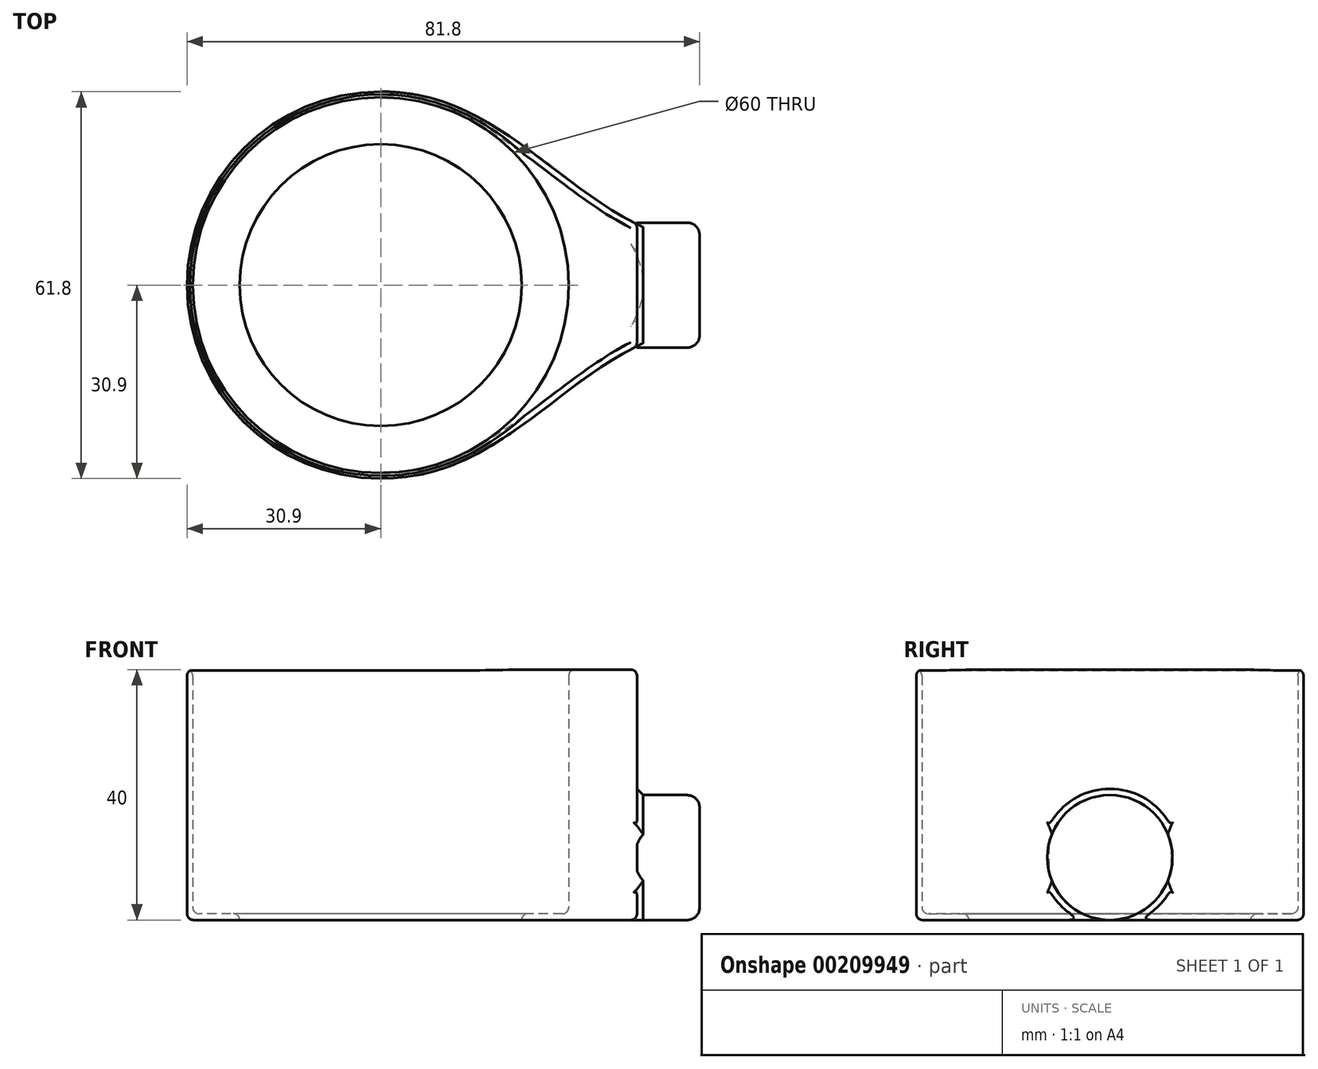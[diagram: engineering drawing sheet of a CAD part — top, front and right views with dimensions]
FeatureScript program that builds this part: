
annotation { "Feature Type Name" : "Feature", "Feature Type Description" : "" }
export const myFeature = defineFeature(function(context is Context, id is Id, definition is map)
    precondition{}
    {
        {
            var Q0;
            Q0=qCreatedBy(makeId("Right.planeOp"),FACE);
            var sketch = newSketch(context, id + "F0", { "sketchPlane" : qUnion([Q0])});
            skCircle(sketch, "E0", {"center": v(0, 0) * mm, "radius": 9.97 * mm});
            skSolve(sketch);
        }
        {
            var Q0;
            Q0=makeQuery(id+"F0.imprint","IMPRINT",FACE,{"disambiguationData":[TD([[makeQuery(id+"F0.imprint","IMPRINT",EDGE,{"derivedFrom":sQuery(id+"F0.wireOp",EDGE,"E0")}),1.0]])]});
            extrude(context, id + "F1", {"entities" : qUnion([Q0]), "depth" : 10 * mm});
        }
        {
            var Q0;
            Q0=qCreatedBy(makeId("Top.planeOp"),FACE);
            var sketch = newSketch(context, id + "F2", { "sketchPlane" : qUnion([Q0])});
            skCircle(sketch, "E1", {"center": v(-40.9, 0) * mm, "radius": 30.9 * mm});
            skLineSegment(sketch, "E2", {"start": v(-40.9, 0) * mm, "end": v(-40.9, 30.9) * mm, "construction": true});
            skLineSegment(sketch, "E3", {"start": v(-40.9, 0) * mm, "end": v(-40.9, -30.9) * mm, "construction": true});
            skCircle(sketch, "E4", {"center": v(-40.9, 0) * mm, "radius": 9.75 * mm, "construction": true});
            skPoint(sketch, "E5", {"position": v(-40.9, 9.75) * mm});
            skPoint(sketch, "E6", {"position": v(-40.9, -9.75) * mm});
            skFitSpline(sketch, "E7", {"points": [v(-40.9, 30.9) * mm, v(0, 9.75) * mm], "startDerivative": vector(52.12, 0.26) * mm, "endDerivative": vector(41.55, -20.66) * mm});
            skLineSegment(sketch, "E8", {"start": v(-40.9, 0) * mm, "end": v(-10, 0) * mm, "construction": true});
            skFitSpline(sketch, "E9.MirrorCS", {"points": [v(-40.9, -30.9) * mm, v(0, -9.75) * mm], "startDerivative": vector(52.12, -0.26) * mm, "endDerivative": vector(41.55, 20.66) * mm});
            skLineSegment(sketch, "E10", {"start": v(0, -9.75) * mm, "end": v(0, 9.75) * mm});
            skCircle(sketch, "E11", {"center": v(-40.9, 0) * mm, "radius": 30 * mm});
            skCircle(sketch, "E12", {"center": v(-40.9, 0) * mm, "radius": 22.5 * mm});
            skSolve(sketch);
        }
        {
            var Q0;
            Q0=makeQuery(id+"F1.opExtrude","SWEPT_BODY",BODY,{"disambiguationData":[OSD([sQuery(id+"F0.wireOp",EDGE,"E0")])]});
            transform(context, id + "F3", {"entities" : qUnion([Q0]), "transformType" : TransformType.TRANSLATION_3D, "dx" : 0 * mm, "dy" : 0 * mm, "dz" : (19.95 / 2) * mm, "makeCopy" : false});
        }
        {
            var Q0;
            Q0=makeQuery(id+"F2.imprint","IMPRINT",FACE,{"disambiguationData":[TD([[makeQuery(id+"F2.imprint","IMPRINT",EDGE,{"derivedFrom":sQuery(id+"F2.wireOp",EDGE,"E11")}),1.0]])]});
            extrude(context, id + "F4", {"entities" : qUnion([Q0]), "depth" : 1 * mm});
        }
        {
            var Q0;
            Q0=makeQuery(id+"F2.imprint","IMPRINT",FACE,{"disambiguationData":[TD([[makeQuery(id+"F2.imprint","IMPRINT",EDGE,{"derivedFrom":sQuery(id+"F2.wireOp",EDGE,"E11")}),-1.0]])]});
            var Q1;
            {var subQ0=sQuery(id+"F2.wireOp",EDGE,"E7");Q1=makeQuery(id+"F2.imprint","IMPRINT",FACE,{"disambiguationData":[TD([[makeQuery(id+"F2.imprint","IMPRINT",EDGE,{"derivedFrom":subQ0}),-1.0]])]});}
            extrude(context, id + "F5", {"entities" : qUnion([Q0, Q1]), "operationType" : NewBodyOperationType.ADD, "depth" : 40 * mm});
        }
        {
            var Q0;
            Q0=makeQuery(id+"F1.opExtrude","CAP_FACE",FACE,{"disambiguationData":[OSD([sQuery(id+"F0.wireOp",EDGE,"E0")])],"isStart":false});
            fillet(context, id + "F6", {"entities" : qUnion([Q0]), "radius" : 2 * mm, "tangentPropagation" : true, "allowEdgeOverflow" : false});
        }
        {
            var Q0;
            {var subQ0=sQuery(id+"F0.wireOp",EDGE,"E0");var subQ1=makeQuery(id+"F1.opExtrude","SWEPT_FACE",FACE,{"disambiguationData":[OSD([subQ0])]});var subQ2=makeQuery(id+"F5.opExtrude","SWEPT_FACE",FACE,{"disambiguationData":[OSD([sQuery(id+"F2.wireOp",EDGE,"E10")])]});Q0=makeQuery(id+"F5.boolean.opBoolean","SPLIT",EDGE,{"disambiguationData":[topologyDisambiguationEdgeConnected([subQ1,subQ2]),TD([subQ1,makeQuery(id+"F1.opExtrude","CAP_FACE",FACE,{"disambiguationData":[OSD([subQ0])],"isStart":true}),makeQuery(id+"F5.opExtrude","SWEPT_FACE",FACE,{"disambiguationData":[OSD([sQuery(id+"F2.wireOp",EDGE,"E7")])]}),makeQuery(id+"F5.opExtrude","SWEPT_FACE",FACE,{"disambiguationData":[OSD([sQuery(id+"F2.wireOp",EDGE,"E9.MirrorCS")])]}),subQ2])],"derivedFrom":makeQuery(id+"F1.opExtrude","CAP_EDGE",EDGE,{"disambiguationData":[OSD([subQ0])],"isStart":true})});}
            var Q1;
            {var subQ0=sQuery(id+"F2.wireOp",EDGE,"E11");var subQ1=sQuery(id+"F2.wireOp",EDGE,"E10");var subQ2=sQuery(id+"F2.wireOp",EDGE,"E7");var subQ3=sQuery(id+"F0.wireOp",EDGE,"E0");var subQ4=makeQuery(id+"F1.opExtrude","SWEPT_FACE",FACE,{"disambiguationData":[OSD([subQ3])]});var subQ5=makeQuery(id+"F5.opExtrude","SWEPT_FACE",FACE,{"disambiguationData":[OSD([subQ1])]});Q1=makeQuery(id+"F5.boolean.opBoolean","SPLIT",EDGE,{"disambiguationData":[topologyDisambiguationEdgeConnected([subQ4,subQ5]),TD([subQ4,makeQuery(id+"F1.opExtrude","CAP_FACE",FACE,{"disambiguationData":[OSD([subQ3])],"isStart":true}),makeQuery(id+"F4.opExtrude","CAP_FACE",FACE,{"disambiguationData":[OSD([subQ0,sQuery(id+"F2.wireOp",EDGE,"E12")])],"isStart":true}),makeQuery(id+"F5.opExtrude","CAP_FACE",FACE,{"disambiguationData":[OSD([sQuery(id+"F2.wireOp",EDGE,"E1"),subQ2,sQuery(id+"F2.wireOp",EDGE,"E9.MirrorCS"),subQ1,subQ0])],"isStart":true}),makeQuery(id+"F5.opExtrude","SWEPT_FACE",FACE,{"disambiguationData":[OSD([subQ2])]}),subQ5])],"derivedFrom":makeQuery(id+"F1.opExtrude","CAP_EDGE",EDGE,{"disambiguationData":[OSD([subQ3])],"isStart":true})});}
            var Q2;
            {var subQ0=sQuery(id+"F2.wireOp",EDGE,"E11");var subQ1=sQuery(id+"F2.wireOp",EDGE,"E10");var subQ2=sQuery(id+"F2.wireOp",EDGE,"E9.MirrorCS");var subQ3=sQuery(id+"F0.wireOp",EDGE,"E0");var subQ4=makeQuery(id+"F1.opExtrude","SWEPT_FACE",FACE,{"disambiguationData":[OSD([subQ3])]});var subQ5=makeQuery(id+"F5.opExtrude","SWEPT_FACE",FACE,{"disambiguationData":[OSD([subQ1])]});Q2=makeQuery(id+"F5.boolean.opBoolean","SPLIT",EDGE,{"disambiguationData":[topologyDisambiguationEdgeConnected([subQ4,subQ5]),TD([subQ4,makeQuery(id+"F1.opExtrude","CAP_FACE",FACE,{"disambiguationData":[OSD([subQ3])],"isStart":true}),makeQuery(id+"F4.opExtrude","CAP_FACE",FACE,{"disambiguationData":[OSD([subQ0,sQuery(id+"F2.wireOp",EDGE,"E12")])],"isStart":true}),makeQuery(id+"F5.opExtrude","CAP_FACE",FACE,{"disambiguationData":[OSD([sQuery(id+"F2.wireOp",EDGE,"E1"),sQuery(id+"F2.wireOp",EDGE,"E7"),subQ2,subQ1,subQ0])],"isStart":true}),makeQuery(id+"F5.opExtrude","SWEPT_FACE",FACE,{"disambiguationData":[OSD([subQ2])]}),subQ5])],"derivedFrom":makeQuery(id+"F1.opExtrude","CAP_EDGE",EDGE,{"disambiguationData":[OSD([subQ3])],"isStart":true})});}
            chamfer(context, id + "F7", {"entities" : qUnion([Q0, Q1, Q2]), "width" : 1 * mm, "tangentPropagation" : true});
        }
        {
            var Q0;
            {var subQ0=sQuery(id+"F2.wireOp",EDGE,"E9.MirrorCS");var subQ1=makeQuery(id+"F5.opExtrude","SWEPT_FACE",FACE,{"disambiguationData":[OSD([subQ0])]});var subQ2=sQuery(id+"F2.wireOp",EDGE,"E10");var subQ4=makeQuery(id+"F5.opExtrude","SWEPT_FACE",FACE,{"disambiguationData":[OSD([subQ2])]});Q0=makeQuery(id+"F5.boolean.opBoolean","SPLIT",EDGE,{"disambiguationData":[topologyDisambiguationEdgeConnected([subQ1,subQ4]),TD([makeQuery(id+"F5.opExtrude","CAP_FACE",FACE,{"disambiguationData":[OSD([sQuery(id+"F2.wireOp",EDGE,"E1"),sQuery(id+"F2.wireOp",EDGE,"E7"),subQ0,subQ2,sQuery(id+"F2.wireOp",EDGE,"E11")])],"isStart":false})])],"derivedFrom":makeQuery(id+"F5.opExtrude","SWEPT_EDGE",EDGE,{"disambiguationData":[OSD([subQ0,subQ2])]})});}
            var Q1;
            {var subQ0=sQuery(id+"F2.wireOp",EDGE,"E11");var subQ1=sQuery(id+"F2.wireOp",EDGE,"E10");var subQ2=sQuery(id+"F2.wireOp",EDGE,"E9.MirrorCS");var subQ4=makeQuery(id+"F5.opExtrude","SWEPT_FACE",FACE,{"disambiguationData":[OSD([subQ2])]});var subQ5=makeQuery(id+"F5.opExtrude","SWEPT_FACE",FACE,{"disambiguationData":[OSD([subQ1])]});Q1=makeQuery(id+"F5.boolean.opBoolean","SPLIT",EDGE,{"disambiguationData":[topologyDisambiguationEdgeConnected([subQ4,subQ5]),TD([makeQuery(id+"F4.opExtrude","CAP_FACE",FACE,{"disambiguationData":[OSD([subQ0,sQuery(id+"F2.wireOp",EDGE,"E12")])],"isStart":true})])],"derivedFrom":makeQuery(id+"F5.opExtrude","SWEPT_EDGE",EDGE,{"disambiguationData":[OSD([subQ2,subQ1])]})});}
            var Q2;
            {var subQ0=sQuery(id+"F2.wireOp",EDGE,"E11");var subQ1=sQuery(id+"F2.wireOp",EDGE,"E10");var subQ2=sQuery(id+"F2.wireOp",EDGE,"E7");var subQ4=makeQuery(id+"F5.opExtrude","SWEPT_FACE",FACE,{"disambiguationData":[OSD([subQ2])]});var subQ5=makeQuery(id+"F5.opExtrude","SWEPT_FACE",FACE,{"disambiguationData":[OSD([subQ1])]});Q2=makeQuery(id+"F5.boolean.opBoolean","SPLIT",EDGE,{"disambiguationData":[topologyDisambiguationEdgeConnected([subQ4,subQ5]),TD([makeQuery(id+"F4.opExtrude","CAP_FACE",FACE,{"disambiguationData":[OSD([subQ0,sQuery(id+"F2.wireOp",EDGE,"E12")])],"isStart":true})])],"derivedFrom":makeQuery(id+"F5.opExtrude","SWEPT_EDGE",EDGE,{"disambiguationData":[OSD([subQ2,subQ1])]})});}
            var Q3;
            {var subQ0=sQuery(id+"F2.wireOp",EDGE,"E7");var subQ1=makeQuery(id+"F5.opExtrude","SWEPT_FACE",FACE,{"disambiguationData":[OSD([subQ0])]});var subQ3=sQuery(id+"F2.wireOp",EDGE,"E10");var subQ4=makeQuery(id+"F5.opExtrude","SWEPT_FACE",FACE,{"disambiguationData":[OSD([subQ3])]});Q3=makeQuery(id+"F5.boolean.opBoolean","SPLIT",EDGE,{"disambiguationData":[topologyDisambiguationEdgeConnected([subQ1,subQ4]),TD([makeQuery(id+"F5.opExtrude","CAP_FACE",FACE,{"disambiguationData":[OSD([sQuery(id+"F2.wireOp",EDGE,"E1"),subQ0,sQuery(id+"F2.wireOp",EDGE,"E9.MirrorCS"),subQ3,sQuery(id+"F2.wireOp",EDGE,"E11")])],"isStart":false})])],"derivedFrom":makeQuery(id+"F5.opExtrude","SWEPT_EDGE",EDGE,{"disambiguationData":[OSD([subQ0,subQ3])]})});}
            fillet(context, id + "F8", {"entities" : qUnion([Q0, Q1, Q2, Q3]), "radius" : 1 * mm, "tangentPropagation" : true, "allowEdgeOverflow" : false});
        }
        {
            var Q0;
            Q0=makeQuery(id+"F5.opExtrude","CAP_FACE",FACE,{"disambiguationData":[OSD([sQuery(id+"F2.wireOp",EDGE,"E1"),sQuery(id+"F2.wireOp",EDGE,"E7"),sQuery(id+"F2.wireOp",EDGE,"E9.MirrorCS"),sQuery(id+"F2.wireOp",EDGE,"E10"),sQuery(id+"F2.wireOp",EDGE,"E11")])],"isStart":false});
            var Q1;
            Q1=makeQuery(id+"F4.opExtrude","CAP_FACE",FACE,{"disambiguationData":[OSD([sQuery(id+"F2.wireOp",EDGE,"E11"),sQuery(id+"F2.wireOp",EDGE,"E12")])],"isStart":false});
            var Q2;
            Q2=makeQuery(id+"F5.opExtrude","CAP_EDGE",EDGE,{"disambiguationData":[OSD([sQuery(id+"F2.wireOp",EDGE,"E9.MirrorCS")])],"isStart":true});
            var Q3;
            Q3=makeQuery(id+"F5.opExtrude","CAP_EDGE",EDGE,{"disambiguationData":[OSD([sQuery(id+"F2.wireOp",EDGE,"E1")])],"isStart":true});
            var Q4;
            Q4=makeQuery(id+"F5.opExtrude","CAP_EDGE",EDGE,{"disambiguationData":[OSD([sQuery(id+"F2.wireOp",EDGE,"E7")])],"isStart":true});
            fillet(context, id + "F9", {"entities" : qUnion([Q0, Q1, Q2, Q3, Q4]), "radius" : 1 * mm, "tangentPropagation" : true, "allowEdgeOverflow" : false});
        }
    });
